# Revit family: Sanitary_Taps-Mixers_hansgrohe_14080000-Ecos-Single-lever-basin-mixer-M_
name_source: partatom
category: Plumbing Fixtures
revit_build: Autodesk Revit 2015 (Build: 20140903_1530(x64)
units: mm (PartAtom-declared; Revit-internal decimal feet)

## types (1)
- Chrome 000
    BIMobject category = Taps & Mixers
    BIMobject category code = sanitary-taps-mixers
    BIMobject main category = Sanitary
    BIMobject main category code = sanitary
    Brand url = http://www.hansgrohe-int.com
    Default Elevation = 4' - 0"
    Design country = Germany
    Edition number = 1
    GTIN code = https://4011097633404
    IFC Classification = Sanitary Terminal
    Manufacturer country = Germany
    Manufacturer name = hansgrohe
    Material main = Chrome
    Product Guid = ac928e8a-7c72-4dc0-b961-f209abecb41b
    Product SKU = 14080000
    Product data url = https://bimobject.com
    Product family = Ecos
    Product group = Basin mixers
    Product name = 14080000 Ecos Single lever basin mixer M with pop-up waste set
    QR code = http://bimobject.com

## geometry (parser evidence)
native form markers: Sweep x3
no freeform markers — native parametric forms only
